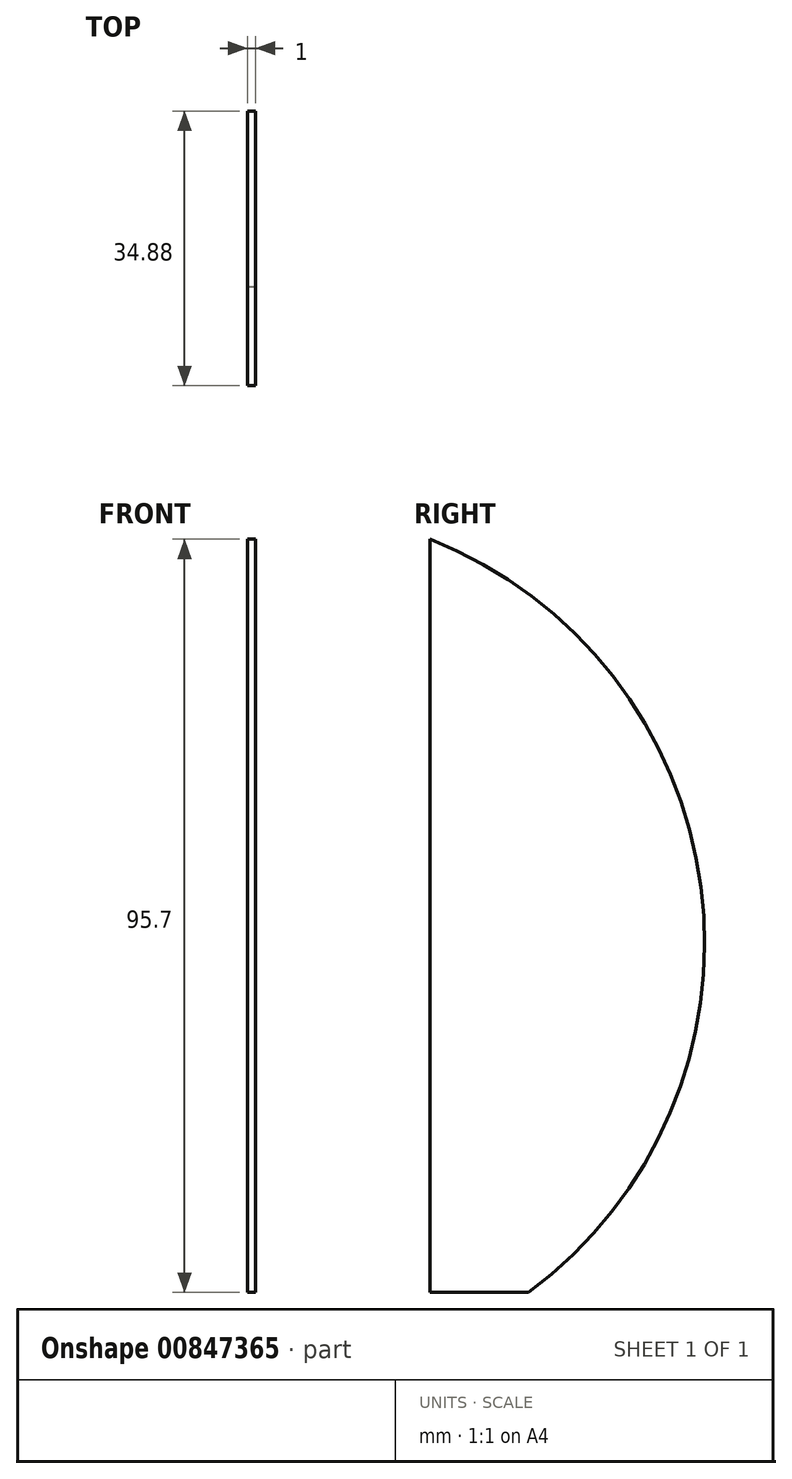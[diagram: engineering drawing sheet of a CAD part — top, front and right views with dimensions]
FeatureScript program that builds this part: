
annotation { "Feature Type Name" : "Feature", "Feature Type Description" : "" }
export const myFeature = defineFeature(function(context is Context, id is Id, definition is map)
    precondition{}
    {
        {
            var Q0;
            Q0=qCreatedBy(makeId("Right.planeOp"),FACE);
            var sketch = newSketch(context, id + "F0", { "sketchPlane" : qUnion([Q0])});
            skLineSegment(sketch, "E0", {"start": v(0, 0) * mm, "end": v(0, 95.7) * mm});
            skArc(sketch, "E1", {"start": v(12.52, 0) * mm, "mid": v(34.41, 51.53) * mm, "end": v(0, 95.7) * mm});
            skLineSegment(sketch, "E2", {"start": v(0, 0) * mm, "end": v(12.52, 0) * mm});
            skSolve(sketch);
        }
        {
            var Q0;
            Q0=makeQuery(id+"F0.imprint","IMPRINT",FACE,{"disambiguationData":[TD([[makeQuery(id+"F0.imprint","IMPRINT",EDGE,{"derivedFrom":sQuery(id+"F0.wireOp",EDGE,"E0")}),-1.0]])]});
            extrude(context, id + "F1", {"entities" : qUnion([Q0]), "depth" : 1 * mm, "offsetDistance" : 25 * mm});
        }
    });
